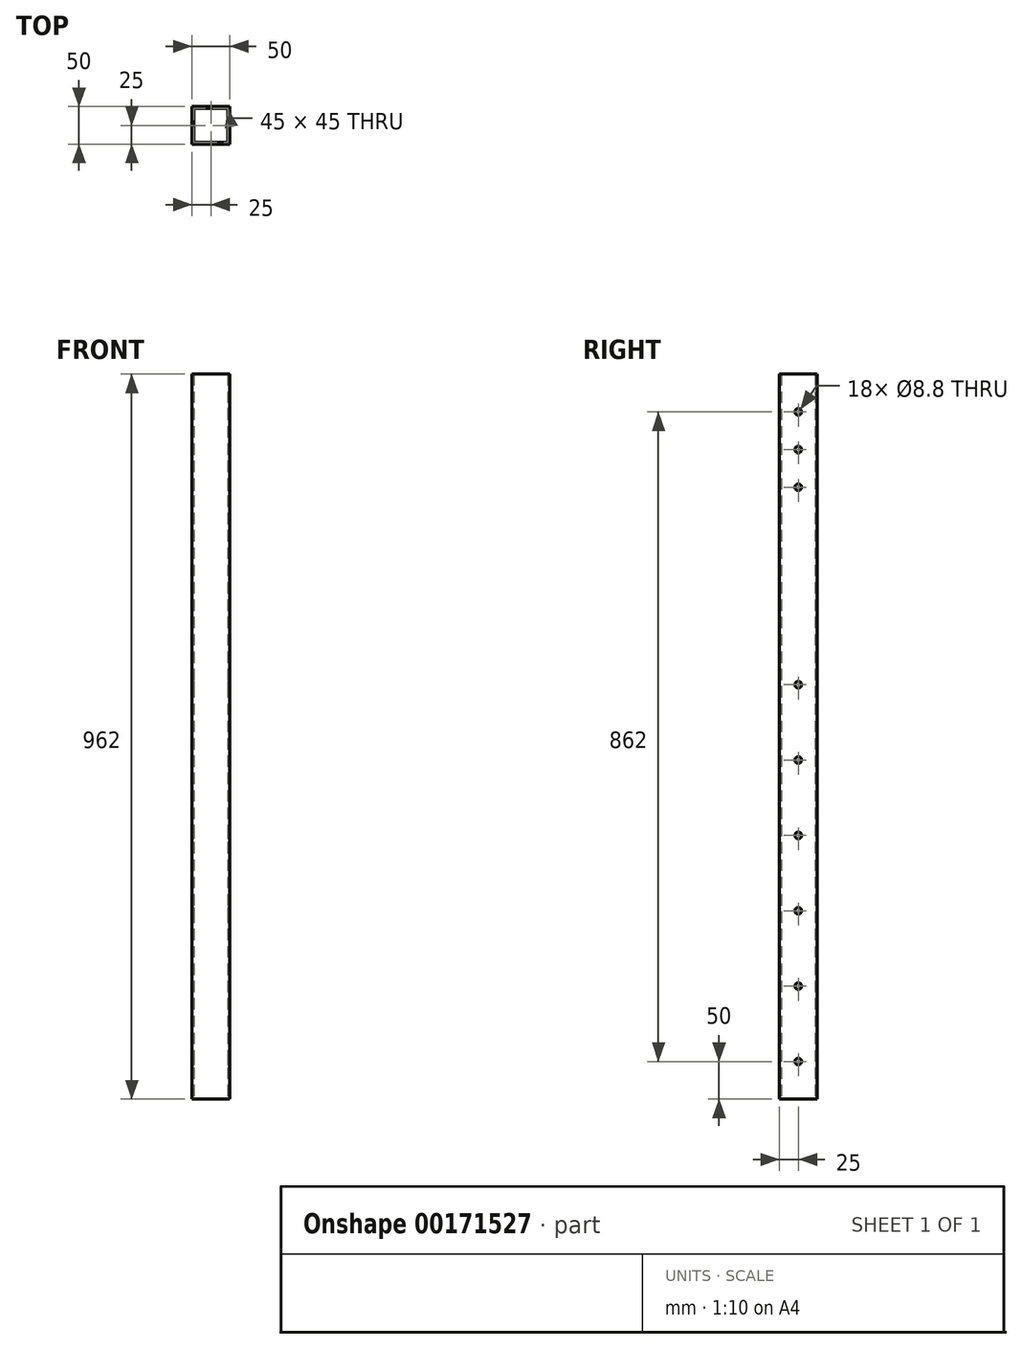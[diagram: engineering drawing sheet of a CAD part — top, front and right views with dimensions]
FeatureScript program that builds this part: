
annotation { "Feature Type Name" : "Feature", "Feature Type Description" : "" }
export const myFeature = defineFeature(function(context is Context, id is Id, definition is map)
    precondition{}
    {
        {
            var Q0;
            Q0=qCreatedBy(makeId("Top.planeOp"),FACE);
            var sketch = newSketch(context, id + "F0", { "sketchPlane" : qUnion([Q0])});
            skLineSegment(sketch, "E0.bottom", {"start": v(25, -25) * mm, "end": v(-25, -25) * mm});
            skLineSegment(sketch, "E0.top", {"start": v(25, 25) * mm, "end": v(-25, 25) * mm});
            skLineSegment(sketch, "E0.left", {"start": v(25, -25) * mm, "end": v(25, 25) * mm});
            skLineSegment(sketch, "E0.right", {"start": v(-25, -25) * mm, "end": v(-25, 25) * mm});
            skPoint(sketch, "E0.middle", {"position": v(0, 0) * mm});
            skLineSegment(sketch, "E1.bottom", {"start": v(22.5, -22.5) * mm, "end": v(-22.5, -22.5) * mm});
            skLineSegment(sketch, "E1.top", {"start": v(22.5, 22.5) * mm, "end": v(-22.5, 22.5) * mm});
            skLineSegment(sketch, "E1.left", {"start": v(22.5, -22.5) * mm, "end": v(22.5, 22.5) * mm});
            skLineSegment(sketch, "E1.right", {"start": v(-22.5, -22.5) * mm, "end": v(-22.5, 22.5) * mm});
            skSolve(sketch);
        }
        {
            var Q0;
            Q0=makeQuery(id+"F0.imprint","IMPRINT",FACE,{"disambiguationData":[TD([[makeQuery(id+"F0.imprint","IMPRINT",EDGE,{"derivedFrom":sQuery(id+"F0.wireOp",EDGE,"E0.bottom")}),-1.0]])]});
            extrude(context, id + "F1", {"entities" : qUnion([Q0]), "depth" : 962 * mm});
        }
        {
            var Q0;
            Q0=makeQuery(id+"F1.opExtrude","SWEPT_FACE",FACE,{"disambiguationData":[OSD([sQuery(id+"F0.wireOp",EDGE,"E0.right")])]});
            var sketch = newSketch(context, id + "F2", { "sketchPlane" : qUnion([Q0])});
            skPoint(sketch, "E2", {"position": v(0, 912) * mm});
            skPoint(sketch, "E2.positionSnap0", {"position": v(0, 962) * mm});
            skPoint(sketch, "E3", {"position": v(0, 862) * mm});
            skPoint(sketch, "E4", {"position": v(0, 812) * mm});
            skPoint(sketch, "E5", {"position": v(0, 50) * mm});
            skPoint(sketch, "E5.positionSnap0", {"position": v(0, 0) * mm});
            skPoint(sketch, "E6", {"position": v(0, 150) * mm});
            skPoint(sketch, "E7", {"position": v(0, 250) * mm});
            skPoint(sketch, "E8", {"position": v(0, 350) * mm});
            skPoint(sketch, "E9", {"position": v(0, 450) * mm});
            skPoint(sketch, "E10", {"position": v(0, 550) * mm});
            skSolve(sketch);
        }
        {
            var Q0;
            Q0=sQuery(id+"F2.wireOp",VERTEX,"E8");
            var Q1;
            Q1=sQuery(id+"F2.wireOp",VERTEX,"E9");
            var Q2;
            Q2=sQuery(id+"F2.wireOp",VERTEX,"E10");
            var Q3;
            Q3=sQuery(id+"F2.wireOp",VERTEX,"E7");
            var Q4;
            Q4=sQuery(id+"F2.wireOp",VERTEX,"E6");
            var Q5;
            Q5=sQuery(id+"F2.wireOp",VERTEX,"E5");
            var Q6;
            Q6=sQuery(id+"F2.wireOp",VERTEX,"E4");
            var Q7;
            Q7=sQuery(id+"F2.wireOp",VERTEX,"E2");
            var Q8;
            Q8=sQuery(id+"F2.wireOp",VERTEX,"E3");
            var Q9;
            Q9=makeQuery(id+"F1.opExtrude","SWEPT_BODY",BODY,{"disambiguationData":[OSD([sQuery(id+"F0.wireOp",EDGE,"E0.bottom"),sQuery(id+"F0.wireOp",EDGE,"E0.top"),sQuery(id+"F0.wireOp",EDGE,"E0.left"),sQuery(id+"F0.wireOp",EDGE,"E0.right"),sQuery(id+"F0.wireOp",EDGE,"E1.bottom"),sQuery(id+"F0.wireOp",EDGE,"E1.top"),sQuery(id+"F0.wireOp",EDGE,"E1.left"),sQuery(id+"F0.wireOp",EDGE,"E1.right")])]});
            hole(context, id + "F3", {"style" : HoleStyle.SIMPLE, "endStyle" : HoleEndStyle.THROUGH, "standardTappedOrClearance" : lookupTablePath({ "standard" : "ISO", "fit" : "Normal", "size" : "M8", "type" : "Clearance" }), "standardBlindInLast" : lookupTablePath({ "fit" : "Standard", "standard" : "ISO", "size" : "M8", "type" : "Clearance" }), "holeDiameter" : 8.8 * mm, "locations" : qUnion([Q0, Q1, Q2, Q3, Q4, Q5, Q6, Q7, Q8]), "scope" : qUnion([Q9]), "isTappedThrough" : true});
        }
    });
